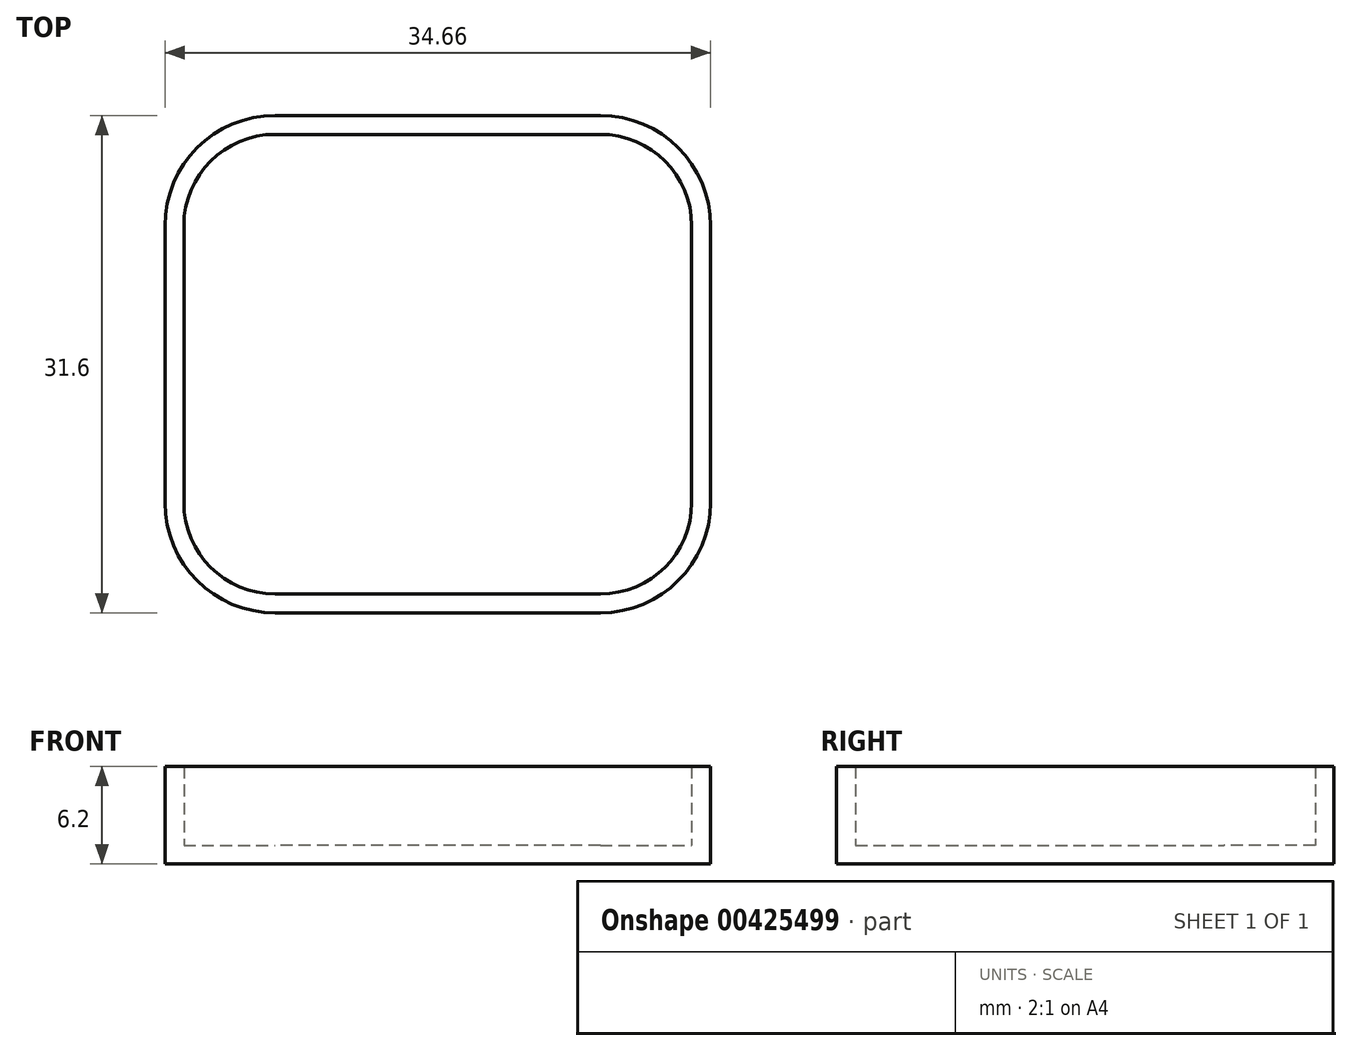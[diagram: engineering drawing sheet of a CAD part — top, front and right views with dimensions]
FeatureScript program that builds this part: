
annotation { "Feature Type Name" : "Feature", "Feature Type Description" : "" }
export const myFeature = defineFeature(function(context is Context, id is Id, definition is map)
    precondition{}
    {
        {
            var Q0;
            Q0=qCreatedBy(makeId("Top.planeOp"),FACE);
            var sketch = newSketch(context, id + "F0", { "sketchPlane" : qUnion([Q0])});
            skLineSegment(sketch, "E0.bottom", {"start": v(10.33, -15.8) * mm, "end": v(-10.33, -15.8) * mm});
            skLineSegment(sketch, "E0.top", {"start": v(10.33, 15.8) * mm, "end": v(-10.33, 15.8) * mm});
            skLineSegment(sketch, "E0.left", {"start": v(17.32, -8.8) * mm, "end": v(17.32, 8.8) * mm});
            skLineSegment(sketch, "E0.right", {"start": v(-17.32, -8.8) * mm, "end": v(-17.32, 8.8) * mm});
            skPoint(sketch, "E0.middle", {"position": v(0, 0) * mm});
            skPoint(sketch, "E1.visualSharp", {"position": v(-17.32, 15.8) * mm});
            skArc(sketch, "E1.filletArc", {"start": v(-10.33, 15.8) * mm, "mid": v(-15.27, 13.75) * mm, "end": v(-17.32, 8.8) * mm});
            skPoint(sketch, "E2.visualSharp", {"position": v(17.32, 15.8) * mm});
            skArc(sketch, "E2.filletArc", {"start": v(17.32, 8.8) * mm, "mid": v(15.27, 13.75) * mm, "end": v(10.33, 15.8) * mm});
            skPoint(sketch, "E3.visualSharp", {"position": v(17.32, -15.8) * mm});
            skArc(sketch, "E3.filletArc", {"start": v(10.33, -15.8) * mm, "mid": v(15.27, -13.75) * mm, "end": v(17.32, -8.8) * mm});
            skPoint(sketch, "E4.visualSharp", {"position": v(-17.33, -15.8) * mm});
            skArc(sketch, "E4.filletArc", {"start": v(-17.33, -8.8) * mm, "mid": v(-15.27, -13.75) * mm, "end": v(-10.33, -15.8) * mm});
            skLineSegment(sketch, "E5.0", {"start": v(16.12, -8.8) * mm, "end": v(16.12, 8.8) * mm});
            skArc(sketch, "E5.1", {"start": v(10.33, -14.6) * mm, "mid": v(14.43, -12.9) * mm, "end": v(16.12, -8.8) * mm});
            skArc(sketch, "E5.2", {"start": v(16.12, 8.8) * mm, "mid": v(14.43, 12.9) * mm, "end": v(10.33, 14.6) * mm});
            skLineSegment(sketch, "E5.3", {"start": v(10.33, -14.6) * mm, "end": v(-10.33, -14.6) * mm});
            skLineSegment(sketch, "E5.4", {"start": v(10.33, 14.6) * mm, "end": v(-10.33, 14.6) * mm});
            skArc(sketch, "E5.5", {"start": v(-10.33, 14.6) * mm, "mid": v(-14.43, 12.9) * mm, "end": v(-16.12, 8.8) * mm});
            skLineSegment(sketch, "E5.6", {"start": v(-16.12, -8.8) * mm, "end": v(-16.12, 8.8) * mm});
            skArc(sketch, "E5.7", {"start": v(-16.13, -8.8) * mm, "mid": v(-14.43, -12.9) * mm, "end": v(-10.33, -14.6) * mm});
            skSolve(sketch);
        }
        {
            var Q0;
            Q0=makeQuery(id+"F0.imprint","IMPRINT",FACE,{"disambiguationData":[TD([[makeQuery(id+"F0.imprint","IMPRINT",EDGE,{"derivedFrom":sQuery(id+"F0.wireOp",EDGE,"E0.bottom")}),-1.0]])]});
            extrude(context, id + "F1", {"entities" : qUnion([Q0]), "depth" : 6.2 * mm});
        }
        {
            var Q0;
            Q0=makeQuery(id+"F0.imprint","IMPRINT",FACE,{"disambiguationData":[TD([[makeQuery(id+"F0.imprint","IMPRINT",EDGE,{"derivedFrom":sQuery(id+"F0.wireOp",EDGE,"E5.0")}),1.0]])]});
            extrude(context, id + "F2", {"entities" : qUnion([Q0]), "operationType" : NewBodyOperationType.ADD, "depth" : 1.2 * mm});
        }
    });
